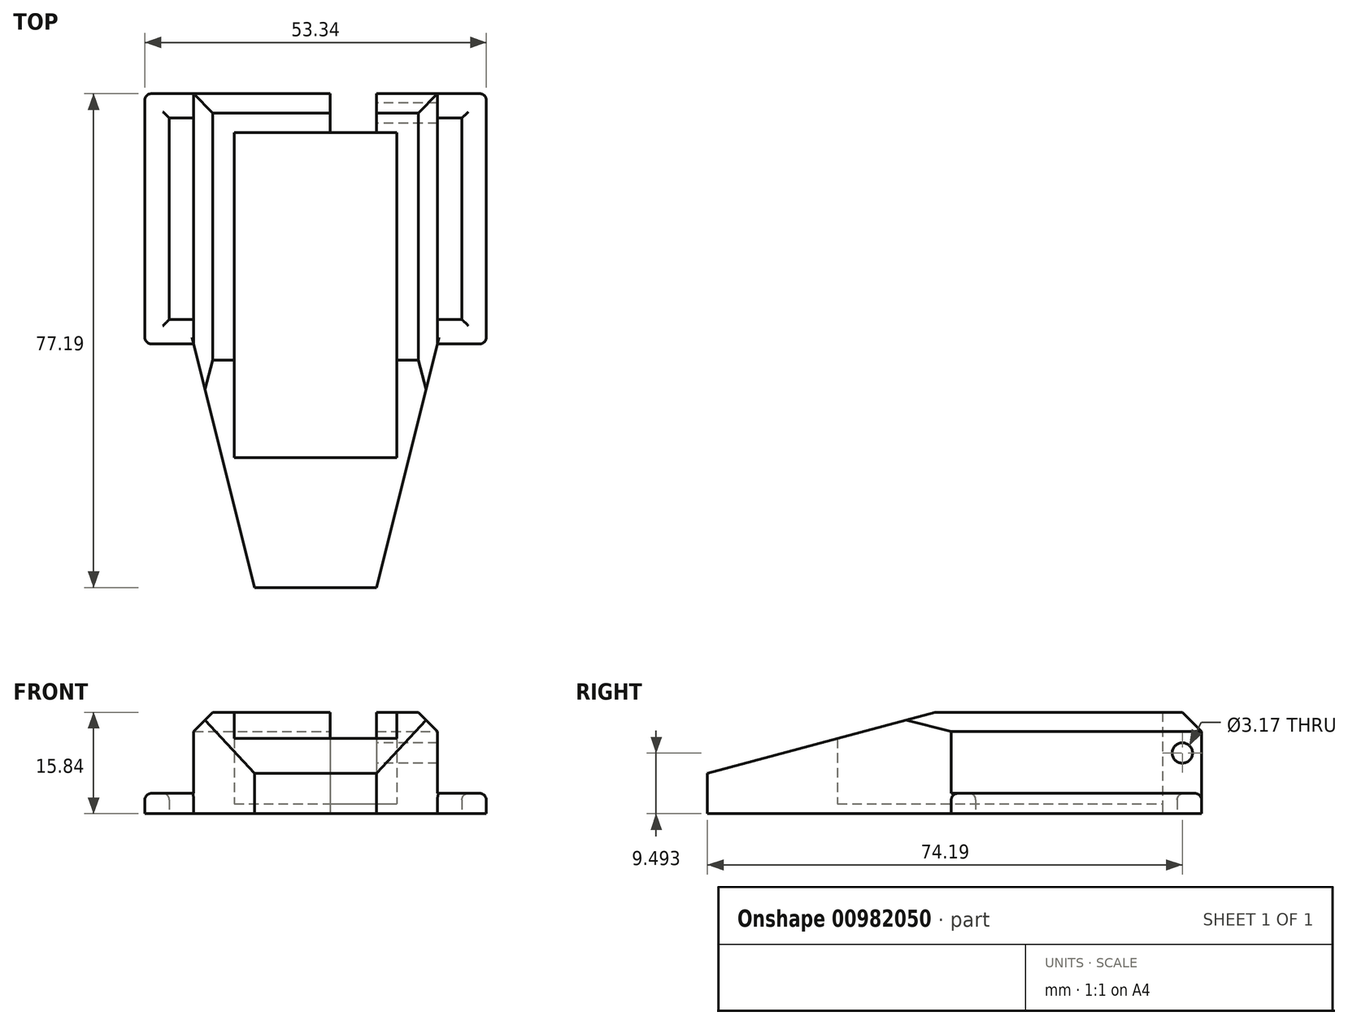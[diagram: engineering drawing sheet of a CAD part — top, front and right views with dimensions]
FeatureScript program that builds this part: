
annotation { "Feature Type Name" : "Feature", "Feature Type Description" : "" }
export const myFeature = defineFeature(function(context is Context, id is Id, definition is map)
    precondition{}
    {
        {
            var Q0;
            Q0=qCreatedBy(makeId("Top.planeOp"),FACE);
            var sketch = newSketch(context, id + "F0", { "sketchPlane" : qUnion([Q0])});
            skLineSegment(sketch, "E0", {"start": v(0, 0) * mm, "end": v(0, 39.09) * mm});
            skLineSegment(sketch, "E1", {"start": v(0, 0) * mm, "end": v(0, -38.1) * mm});
            skLineSegment(sketch, "E2", {"start": v(0, 0) * mm, "end": v(-19.05, 0) * mm});
            skLineSegment(sketch, "E3", {"start": v(0, 0) * mm, "end": v(19.05, 0) * mm});
            skLineSegment(sketch, "E4", {"start": v(-19.05, 0) * mm, "end": v(-19.05, 39.09) * mm});
            skLineSegment(sketch, "E5", {"start": v(19.05, 0) * mm, "end": v(19.05, 39.09) * mm});
            skLineSegment(sketch, "E6", {"start": v(-19.05, 39.09) * mm, "end": v(19.05, 39.09) * mm});
            skLineSegment(sketch, "E7", {"start": v(-19.05, 0) * mm, "end": v(-19.05, -38.1) * mm});
            skLineSegment(sketch, "E8", {"start": v(19.05, 0) * mm, "end": v(19.05, -38.1) * mm});
            skLineSegment(sketch, "E9", {"start": v(-19.05, -38.1) * mm, "end": v(19.05, -38.1) * mm});
            skLineSegment(sketch, "E10", {"start": v(9.53, 0) * mm, "end": v(9.53, 39.09) * mm});
            skLineSegment(sketch, "E11", {"start": v(-9.53, 0) * mm, "end": v(-9.53, 39.09) * mm});
            skLineSegment(sketch, "E12", {"start": v(9.53, 0) * mm, "end": v(9.53, -38.1) * mm});
            skLineSegment(sketch, "E13", {"start": v(-9.53, 0) * mm, "end": v(-9.53, -38.1) * mm});
            skLineSegment(sketch, "E14", {"start": v(-19.05, 19.54) * mm, "end": v(19.05, 19.54) * mm});
            skLineSegment(sketch, "E15", {"start": v(19.05, -19.05) * mm, "end": v(-19.05, -19.05) * mm});
            skLineSegment(sketch, "E16", {"start": v(-19.05, 0) * mm, "end": v(-9.53, -38.1) * mm});
            skLineSegment(sketch, "E17", {"start": v(19.05, 0) * mm, "end": v(9.53, -38.1) * mm});
            skLineSegment(sketch, "E18", {"start": v(0, 0) * mm, "end": v(12.7, 0) * mm});
            skLineSegment(sketch, "E19", {"start": v(0, 0) * mm, "end": v(-12.7, 0) * mm});
            skLineSegment(sketch, "E20", {"start": v(-12.7, 0) * mm, "end": v(-12.7, 33.02) * mm});
            skLineSegment(sketch, "E21", {"start": v(12.7, 0) * mm, "end": v(12.7, 33.02) * mm});
            skLineSegment(sketch, "E22", {"start": v(-12.7, 0) * mm, "end": v(-12.7, -17.78) * mm});
            skLineSegment(sketch, "E23", {"start": v(12.7, 0) * mm, "end": v(12.7, -17.78) * mm});
            skLineSegment(sketch, "E24", {"start": v(-12.7, 33.02) * mm, "end": v(12.7, 33.02) * mm});
            skLineSegment(sketch, "E25", {"start": v(-12.7, -17.78) * mm, "end": v(12.7, -17.78) * mm});
            skLineSegment(sketch, "E26", {"start": v(-19.05, 39.09) * mm, "end": v(-26.67, 39.09) * mm});
            skLineSegment(sketch, "E27", {"start": v(19.05, 39.09) * mm, "end": v(26.67, 39.09) * mm});
            skLineSegment(sketch, "E28", {"start": v(19.05, 0) * mm, "end": v(26.67, 0) * mm});
            skLineSegment(sketch, "E29", {"start": v(-19.05, 0) * mm, "end": v(-26.67, 0) * mm});
            skLineSegment(sketch, "E30", {"start": v(-26.67, 39.09) * mm, "end": v(-26.67, 0) * mm});
            skLineSegment(sketch, "E31", {"start": v(26.67, 39.09) * mm, "end": v(26.67, 0) * mm});
            skLineSegment(sketch, "E32", {"start": v(-19.05, 39.09) * mm, "end": v(-22.86, 39.09) * mm});
            skPoint(sketch, "E32.endSnap0", {"position": v(-22.86, 39.09) * mm});
            skLineSegment(sketch, "E33", {"start": v(-22.86, 39.09) * mm, "end": v(-22.86, 0) * mm});
            skLineSegment(sketch, "E34", {"start": v(19.05, 39.09) * mm, "end": v(22.86, 39.09) * mm});
            skLineSegment(sketch, "E35", {"start": v(22.86, 39.09) * mm, "end": v(22.86, 0) * mm});
            skLineSegment(sketch, "E36", {"start": v(0, 0) * mm, "end": v(0, 3.81) * mm});
            skPoint(sketch, "E36.endSnap0", {"position": v(0, 33.02) * mm});
            skLineSegment(sketch, "E37", {"start": v(0, 3.8) * mm, "end": v(-26.67, 3.8) * mm});
            skLineSegment(sketch, "E38", {"start": v(0, 3.81) * mm, "end": v(26.67, 3.81) * mm});
            skLineSegment(sketch, "E39", {"start": v(0, 39.09) * mm, "end": v(0, 35.28) * mm});
            skLineSegment(sketch, "E40", {"start": v(0, 35.28) * mm, "end": v(26.67, 35.28) * mm});
            skLineSegment(sketch, "E41", {"start": v(0, 35.28) * mm, "end": v(-26.67, 35.28) * mm});
            skLineSegment(sketch, "E42", {"start": v(2.26, 39.09) * mm, "end": v(2.26, 33.02) * mm});
            skSolve(sketch);
        }
        {
            var Q0;
            {var subQ0=sQuery(id+"F0.wireOp",EDGE,"E14");var subQ1=sQuery(id+"F0.wireOp",EDGE,"E0");var subQ2=makeQuery(id+"F0.imprint","INTERSECT",VERTEX,{"derivedFrom":[subQ1,subQ0]});Q0=makeQuery(id+"F0.imprint","IMPRINT",FACE,{"disambiguationData":[TD([[makeQuery(id+"F0.imprint","IMPRINT",EDGE,{"disambiguationData":[TD([[subQ2,-1.0]])],"derivedFrom":subQ1}),1.0]])]});}
            var Q1;
            {var subQ0=sQuery(id+"F0.wireOp",EDGE,"E24");var subQ1=sQuery(id+"F0.wireOp",EDGE,"E11");var subQ2=makeQuery(id+"F0.imprint","INTERSECT",VERTEX,{"derivedFrom":[subQ1,subQ0]});Q1=makeQuery(id+"F0.imprint","IMPRINT",FACE,{"disambiguationData":[TD([[makeQuery(id+"F0.imprint","IMPRINT",EDGE,{"disambiguationData":[TD([[subQ2,1.0]])],"derivedFrom":subQ1}),1.0]])]});}
            var Q2;
            {var subQ0=sQuery(id+"F0.wireOp",EDGE,"E37");var subQ1=sQuery(id+"F0.wireOp",EDGE,"E11");var subQ2=makeQuery(id+"F0.imprint","INTERSECT",VERTEX,{"derivedFrom":[subQ1,subQ0]});Q2=makeQuery(id+"F0.imprint","IMPRINT",FACE,{"disambiguationData":[TD([[makeQuery(id+"F0.imprint","IMPRINT",EDGE,{"disambiguationData":[TD([[subQ2,-1.0]])],"derivedFrom":subQ1}),1.0]])]});}
            var Q3;
            {var subQ0=sQuery(id+"F0.wireOp",EDGE,"E37");var subQ5=sQuery(id+"F0.wireOp",EDGE,"E11");var subQ6=makeQuery(id+"F0.imprint","INTERSECT",VERTEX,{"derivedFrom":[subQ5,subQ0]});Q3=makeQuery(id+"F0.imprint","IMPRINT",FACE,{"disambiguationData":[TD([[makeQuery(id+"F0.imprint","IMPRINT",EDGE,{"disambiguationData":[TD([[subQ6,-1.0]])],"derivedFrom":subQ5}),-1.0]])]});}
            var Q4;
            {var subQ0=sQuery(id+"F0.wireOp",EDGE,"E38");var subQ5=sQuery(id+"F0.wireOp",EDGE,"E10");var subQ6=makeQuery(id+"F0.imprint","INTERSECT",VERTEX,{"derivedFrom":[subQ5,subQ0]});Q4=makeQuery(id+"F0.imprint","IMPRINT",FACE,{"disambiguationData":[TD([[makeQuery(id+"F0.imprint","IMPRINT",EDGE,{"disambiguationData":[TD([[subQ6,-1.0]])],"derivedFrom":subQ5}),1.0]])]});}
            var Q5;
            {var subQ0=sQuery(id+"F0.wireOp",EDGE,"E38");var subQ1=sQuery(id+"F0.wireOp",EDGE,"E10");var subQ2=makeQuery(id+"F0.imprint","INTERSECT",VERTEX,{"derivedFrom":[subQ1,subQ0]});Q5=makeQuery(id+"F0.imprint","IMPRINT",FACE,{"disambiguationData":[TD([[makeQuery(id+"F0.imprint","IMPRINT",EDGE,{"disambiguationData":[TD([[subQ2,-1.0]])],"derivedFrom":subQ1}),-1.0]])]});}
            var Q6;
            {var subQ0=sQuery(id+"F0.wireOp",EDGE,"E14");var subQ1=sQuery(id+"F0.wireOp",EDGE,"E10");var subQ2=makeQuery(id+"F0.imprint","INTERSECT",VERTEX,{"derivedFrom":[subQ1,subQ0]});Q6=makeQuery(id+"F0.imprint","IMPRINT",FACE,{"disambiguationData":[TD([[makeQuery(id+"F0.imprint","IMPRINT",EDGE,{"disambiguationData":[TD([[subQ2,-1.0]])],"derivedFrom":subQ1}),-1.0]])]});}
            var Q7;
            {var subQ4=sQuery(id+"F0.wireOp",EDGE,"E14");var subQ5=sQuery(id+"F0.wireOp",EDGE,"E0");var subQ6=makeQuery(id+"F0.imprint","INTERSECT",VERTEX,{"derivedFrom":[subQ5,subQ4]});Q7=makeQuery(id+"F0.imprint","IMPRINT",FACE,{"disambiguationData":[TD([[makeQuery(id+"F0.imprint","IMPRINT",EDGE,{"disambiguationData":[TD([[subQ6,-1.0]])],"derivedFrom":subQ5}),-1.0]])]});}
            var Q8;
            {var subQ1=sQuery(id+"F0.wireOp",EDGE,"E1");var subQ3=sQuery(id+"F0.wireOp",EDGE,"E25");var subQ4=makeQuery(id+"F0.imprint","INTERSECT",VERTEX,{"derivedFrom":[subQ1,subQ3]});Q8=makeQuery(id+"F0.imprint","IMPRINT",FACE,{"disambiguationData":[TD([[makeQuery(id+"F0.imprint","IMPRINT",EDGE,{"disambiguationData":[TD([[subQ4,1.0]])],"derivedFrom":subQ3}),1.0]])]});}
            var Q9;
            {var subQ1=sQuery(id+"F0.wireOp",EDGE,"E1");var subQ3=sQuery(id+"F0.wireOp",EDGE,"E25");var subQ4=makeQuery(id+"F0.imprint","INTERSECT",VERTEX,{"derivedFrom":[subQ1,subQ3]});Q9=makeQuery(id+"F0.imprint","IMPRINT",FACE,{"disambiguationData":[TD([[makeQuery(id+"F0.imprint","IMPRINT",EDGE,{"disambiguationData":[TD([[subQ4,-1.0]])],"derivedFrom":subQ3}),1.0]])]});}
            var Q10;
            {var subQ0=sQuery(id+"F0.wireOp",EDGE,"E23");Q10=makeQuery(id+"F0.imprint","IMPRINT",FACE,{"disambiguationData":[TD([[makeQuery(id+"F0.imprint","IMPRINT",EDGE,{"derivedFrom":subQ0}),-1.0]])]});}
            var Q11;
            {var subQ0=sQuery(id+"F0.wireOp",EDGE,"E22");Q11=makeQuery(id+"F0.imprint","IMPRINT",FACE,{"disambiguationData":[TD([[makeQuery(id+"F0.imprint","IMPRINT",EDGE,{"derivedFrom":subQ0}),1.0]])]});}
            var Q12;
            {var subQ3=sQuery(id+"F0.wireOp",EDGE,"E11");var subQ5=sQuery(id+"F0.wireOp",EDGE,"E37");var subQ6=makeQuery(id+"F0.imprint","INTERSECT",VERTEX,{"derivedFrom":[subQ3,subQ5]});Q12=makeQuery(id+"F0.imprint","IMPRINT",FACE,{"disambiguationData":[TD([[makeQuery(id+"F0.imprint","IMPRINT",EDGE,{"disambiguationData":[TD([[subQ6,-1.0]])],"derivedFrom":subQ5}),1.0]])]});}
            var Q13;
            {var subQ0=sQuery(id+"F0.wireOp",EDGE,"E37");var subQ5=sQuery(id+"F0.wireOp",EDGE,"E11");var subQ7=makeQuery(id+"F0.imprint","INTERSECT",VERTEX,{"derivedFrom":[subQ5,subQ0]});Q13=makeQuery(id+"F0.imprint","IMPRINT",FACE,{"disambiguationData":[TD([[makeQuery(id+"F0.imprint","IMPRINT",EDGE,{"disambiguationData":[TD([[subQ7,1.0]])],"derivedFrom":subQ5}),-1.0]])]});}
            var Q14;
            {var subQ0=sQuery(id+"F0.wireOp",EDGE,"E38");var subQ5=sQuery(id+"F0.wireOp",EDGE,"E10");var subQ7=makeQuery(id+"F0.imprint","INTERSECT",VERTEX,{"derivedFrom":[subQ5,subQ0]});Q14=makeQuery(id+"F0.imprint","IMPRINT",FACE,{"disambiguationData":[TD([[makeQuery(id+"F0.imprint","IMPRINT",EDGE,{"disambiguationData":[TD([[subQ7,1.0]])],"derivedFrom":subQ5}),1.0]])]});}
            var Q15;
            {var subQ3=sQuery(id+"F0.wireOp",EDGE,"E10");var subQ5=sQuery(id+"F0.wireOp",EDGE,"E38");var subQ6=makeQuery(id+"F0.imprint","INTERSECT",VERTEX,{"derivedFrom":[subQ3,subQ5]});Q15=makeQuery(id+"F0.imprint","IMPRINT",FACE,{"disambiguationData":[TD([[makeQuery(id+"F0.imprint","IMPRINT",EDGE,{"disambiguationData":[TD([[subQ6,-1.0]])],"derivedFrom":subQ5}),-1.0]])]});}
            extrude(context, id + "F1", {"entities" : qUnion([Q0, Q1, Q2, Q3, Q4, Q5, Q6, Q7, Q8, Q9, Q10, Q11, Q12, Q13, Q14, Q15]), "depth" : 1.56 * mm, "offsetDistance" : 25.4 * mm});
        }
        {
            var Q0;
            {var subQ3=sQuery(id+"F0.wireOp",EDGE,"E14");var subQ5=sQuery(id+"F0.wireOp",EDGE,"E4");var subQ6=makeQuery(id+"F0.imprint","INTERSECT",VERTEX,{"derivedFrom":[subQ5,subQ3]});Q0=makeQuery(id+"F0.imprint","IMPRINT",FACE,{"disambiguationData":[TD([[makeQuery(id+"F0.imprint","IMPRINT",EDGE,{"disambiguationData":[TD([[subQ6,-1.0]])],"derivedFrom":subQ5}),-1.0]])]});}
            var Q1;
            {var subQ3=sQuery(id+"F0.wireOp",EDGE,"E41");var subQ5=sQuery(id+"F0.wireOp",EDGE,"E11");var subQ7=makeQuery(id+"F0.imprint","INTERSECT",VERTEX,{"derivedFrom":[subQ5,subQ3]});Q1=makeQuery(id+"F0.imprint","IMPRINT",FACE,{"disambiguationData":[TD([[makeQuery(id+"F0.imprint","IMPRINT",EDGE,{"disambiguationData":[TD([[subQ7,-1.0]])],"derivedFrom":subQ5}),1.0]])]});}
            var Q2;
            {var subQ0=sQuery(id+"F0.wireOp",EDGE,"E26");var subQ5=sQuery(id+"F0.wireOp",EDGE,"E33");var subQ6=makeQuery(id+"F0.imprint","INTERSECT",VERTEX,{"derivedFrom":[subQ0,subQ5]});Q2=makeQuery(id+"F0.imprint","IMPRINT",FACE,{"disambiguationData":[TD([[makeQuery(id+"F0.imprint","IMPRINT",EDGE,{"disambiguationData":[TD([[subQ6,-1.0]])],"derivedFrom":subQ5}),1.0]])]});}
            var Q3;
            {var subQ0=sQuery(id+"F0.wireOp",EDGE,"E33");var subQ1=sQuery(id+"F0.wireOp",EDGE,"E26");var subQ2=makeQuery(id+"F0.imprint","INTERSECT",VERTEX,{"derivedFrom":[subQ1,subQ0]});Q3=makeQuery(id+"F0.imprint","IMPRINT",FACE,{"disambiguationData":[TD([[makeQuery(id+"F0.imprint","IMPRINT",EDGE,{"disambiguationData":[TD([[subQ2,-1.0]])],"derivedFrom":subQ1}),1.0]])]});}
            var Q4;
            {var subQ0=sQuery(id+"F0.wireOp",EDGE,"E41");var subQ1=sQuery(id+"F0.wireOp",EDGE,"E30");var subQ2=makeQuery(id+"F0.imprint","INTERSECT",VERTEX,{"derivedFrom":[subQ1,subQ0]});Q4=makeQuery(id+"F0.imprint","IMPRINT",FACE,{"disambiguationData":[TD([[makeQuery(id+"F0.imprint","IMPRINT",EDGE,{"disambiguationData":[TD([[subQ2,-1.0]])],"derivedFrom":subQ1}),1.0]])]});}
            var Q5;
            {var subQ0=sQuery(id+"F0.wireOp",EDGE,"E30");var subQ1=sQuery(id+"F0.wireOp",EDGE,"E29");var subQ2=makeQuery(id+"F0.imprint","INTERSECT",VERTEX,{"derivedFrom":[subQ1,subQ0]});Q5=makeQuery(id+"F0.imprint","IMPRINT",FACE,{"disambiguationData":[TD([[makeQuery(id+"F0.imprint","IMPRINT",EDGE,{"disambiguationData":[TD([[subQ2,1.0]])],"derivedFrom":subQ1}),-1.0]])]});}
            var Q6;
            {var subQ3=sQuery(id+"F0.wireOp",EDGE,"E29");var subQ5=sQuery(id+"F0.wireOp",EDGE,"E33");var subQ7=makeQuery(id+"F0.imprint","INTERSECT",VERTEX,{"derivedFrom":[subQ3,subQ5]});Q6=makeQuery(id+"F0.imprint","IMPRINT",FACE,{"disambiguationData":[TD([[makeQuery(id+"F0.imprint","IMPRINT",EDGE,{"disambiguationData":[TD([[subQ7,1.0]])],"derivedFrom":subQ5}),1.0]])]});}
            var Q7;
            {var subQ3=sQuery(id+"F0.wireOp",EDGE,"E4");var subQ5=sQuery(id+"F0.wireOp",EDGE,"E37");var subQ7=makeQuery(id+"F0.imprint","INTERSECT",VERTEX,{"derivedFrom":[subQ3,subQ5]});Q7=makeQuery(id+"F0.imprint","IMPRINT",FACE,{"disambiguationData":[TD([[makeQuery(id+"F0.imprint","IMPRINT",EDGE,{"disambiguationData":[TD([[subQ7,1.0]])],"derivedFrom":subQ5}),1.0]])]});}
            var Q8;
            {var subQ0=sQuery(id+"F0.wireOp",EDGE,"E37");var subQ1=sQuery(id+"F0.wireOp",EDGE,"E4");var subQ2=makeQuery(id+"F0.imprint","INTERSECT",VERTEX,{"derivedFrom":[subQ1,subQ0]});Q8=makeQuery(id+"F0.imprint","IMPRINT",FACE,{"disambiguationData":[TD([[makeQuery(id+"F0.imprint","IMPRINT",EDGE,{"disambiguationData":[TD([[subQ2,-1.0]])],"derivedFrom":subQ1}),-1.0]])]});}
            var Q9;
            {var subQ9=sQuery(id+"F0.wireOp",EDGE,"E22");Q9=makeQuery(id+"F0.imprint","IMPRINT",FACE,{"disambiguationData":[TD([[makeQuery(id+"F0.imprint","IMPRINT",EDGE,{"derivedFrom":subQ9}),-1.0]])]});}
            var Q10;
            {var subQ0=sQuery(id+"F0.wireOp",EDGE,"E15");var subQ1=sQuery(id+"F0.wireOp",EDGE,"E1");var subQ2=makeQuery(id+"F0.imprint","INTERSECT",VERTEX,{"derivedFrom":[subQ1,subQ0]});Q10=makeQuery(id+"F0.imprint","IMPRINT",FACE,{"disambiguationData":[TD([[makeQuery(id+"F0.imprint","IMPRINT",EDGE,{"disambiguationData":[TD([[subQ2,1.0]])],"derivedFrom":subQ1}),-1.0]])]});}
            var Q11;
            {var subQ0=sQuery(id+"F0.wireOp",EDGE,"E15");var subQ1=sQuery(id+"F0.wireOp",EDGE,"E1");var subQ2=makeQuery(id+"F0.imprint","INTERSECT",VERTEX,{"derivedFrom":[subQ1,subQ0]});Q11=makeQuery(id+"F0.imprint","IMPRINT",FACE,{"disambiguationData":[TD([[makeQuery(id+"F0.imprint","IMPRINT",EDGE,{"disambiguationData":[TD([[subQ2,1.0]])],"derivedFrom":subQ1}),1.0]])]});}
            var Q12;
            {var subQ9=sQuery(id+"F0.wireOp",EDGE,"E23");Q12=makeQuery(id+"F0.imprint","IMPRINT",FACE,{"disambiguationData":[TD([[makeQuery(id+"F0.imprint","IMPRINT",EDGE,{"derivedFrom":subQ9}),1.0]])]});}
            var Q13;
            {var subQ0=sQuery(id+"F0.wireOp",EDGE,"E15");var subQ1=sQuery(id+"F0.wireOp",EDGE,"E12");var subQ2=makeQuery(id+"F0.imprint","INTERSECT",VERTEX,{"derivedFrom":[subQ1,subQ0]});Q13=makeQuery(id+"F0.imprint","IMPRINT",FACE,{"disambiguationData":[TD([[makeQuery(id+"F0.imprint","IMPRINT",EDGE,{"disambiguationData":[TD([[subQ2,1.0]])],"derivedFrom":subQ0}),1.0]])]});}
            var Q14;
            {var subQ1=sQuery(id+"F0.wireOp",EDGE,"E13");var subQ3=sQuery(id+"F0.wireOp",EDGE,"E15");var subQ4=makeQuery(id+"F0.imprint","INTERSECT",VERTEX,{"derivedFrom":[subQ1,subQ3]});Q14=makeQuery(id+"F0.imprint","IMPRINT",FACE,{"disambiguationData":[TD([[makeQuery(id+"F0.imprint","IMPRINT",EDGE,{"disambiguationData":[TD([[subQ4,-1.0]])],"derivedFrom":subQ3}),1.0]])]});}
            var Q15;
            {var subQ0=sQuery(id+"F0.wireOp",EDGE,"E15");var subQ1=sQuery(id+"F0.wireOp",EDGE,"E1");var subQ2=makeQuery(id+"F0.imprint","INTERSECT",VERTEX,{"derivedFrom":[subQ1,subQ0]});Q15=makeQuery(id+"F0.imprint","IMPRINT",FACE,{"disambiguationData":[TD([[makeQuery(id+"F0.imprint","IMPRINT",EDGE,{"disambiguationData":[TD([[subQ2,-1.0]])],"derivedFrom":subQ1}),-1.0]])]});}
            var Q16;
            {var subQ0=sQuery(id+"F0.wireOp",EDGE,"E15");var subQ1=sQuery(id+"F0.wireOp",EDGE,"E1");var subQ2=makeQuery(id+"F0.imprint","INTERSECT",VERTEX,{"derivedFrom":[subQ1,subQ0]});Q16=makeQuery(id+"F0.imprint","IMPRINT",FACE,{"disambiguationData":[TD([[makeQuery(id+"F0.imprint","IMPRINT",EDGE,{"disambiguationData":[TD([[subQ2,-1.0]])],"derivedFrom":subQ1}),1.0]])]});}
            var Q17;
            {var subQ0=sQuery(id+"F0.wireOp",EDGE,"E21");var subQ5=sQuery(id+"F0.wireOp",EDGE,"E38");var subQ6=makeQuery(id+"F0.imprint","INTERSECT",VERTEX,{"derivedFrom":[subQ0,subQ5]});Q17=makeQuery(id+"F0.imprint","IMPRINT",FACE,{"disambiguationData":[TD([[makeQuery(id+"F0.imprint","IMPRINT",EDGE,{"disambiguationData":[TD([[subQ6,-1.0]])],"derivedFrom":subQ5}),-1.0]])]});}
            var Q18;
            {var subQ0=sQuery(id+"F0.wireOp",EDGE,"E14");var subQ1=sQuery(id+"F0.wireOp",EDGE,"E5");var subQ2=makeQuery(id+"F0.imprint","INTERSECT",VERTEX,{"derivedFrom":[subQ1,subQ0]});Q18=makeQuery(id+"F0.imprint","IMPRINT",FACE,{"disambiguationData":[TD([[makeQuery(id+"F0.imprint","IMPRINT",EDGE,{"disambiguationData":[TD([[subQ2,1.0]])],"derivedFrom":subQ1}),1.0]])]});}
            var Q19;
            {var subQ1=sQuery(id+"F0.wireOp",EDGE,"E14");var subQ5=sQuery(id+"F0.wireOp",EDGE,"E5");var subQ6=makeQuery(id+"F0.imprint","INTERSECT",VERTEX,{"derivedFrom":[subQ5,subQ1]});Q19=makeQuery(id+"F0.imprint","IMPRINT",FACE,{"disambiguationData":[TD([[makeQuery(id+"F0.imprint","IMPRINT",EDGE,{"disambiguationData":[TD([[subQ6,-1.0]])],"derivedFrom":subQ5}),1.0]])]});}
            var Q20;
            {var subQ0=sQuery(id+"F0.wireOp",EDGE,"E41");var subQ5=sQuery(id+"F0.wireOp",EDGE,"E11");var subQ6=makeQuery(id+"F0.imprint","INTERSECT",VERTEX,{"derivedFrom":[subQ5,subQ0]});Q20=makeQuery(id+"F0.imprint","IMPRINT",FACE,{"disambiguationData":[TD([[makeQuery(id+"F0.imprint","IMPRINT",EDGE,{"disambiguationData":[TD([[subQ6,1.0]])],"derivedFrom":subQ5}),-1.0]])]});}
            var Q21;
            {var subQ1=sQuery(id+"F0.wireOp",EDGE,"E0");var subQ3=sQuery(id+"F0.wireOp",EDGE,"E6");var subQ4=makeQuery(id+"F0.imprint","INTERSECT",VERTEX,{"derivedFrom":[subQ1,subQ3]});Q21=makeQuery(id+"F0.imprint","IMPRINT",FACE,{"disambiguationData":[TD([[makeQuery(id+"F0.imprint","IMPRINT",EDGE,{"disambiguationData":[TD([[subQ4,1.0]])],"derivedFrom":subQ3}),-1.0]])]});}
            var Q22;
            {var subQ3=sQuery(id+"F0.wireOp",EDGE,"E6");var subQ5=sQuery(id+"F0.wireOp",EDGE,"E42");var subQ6=makeQuery(id+"F0.imprint","INTERSECT",VERTEX,{"derivedFrom":[subQ3,subQ5]});Q22=makeQuery(id+"F0.imprint","IMPRINT",FACE,{"disambiguationData":[TD([[makeQuery(id+"F0.imprint","IMPRINT",EDGE,{"disambiguationData":[TD([[subQ6,1.0]])],"derivedFrom":subQ3}),-1.0]])]});}
            var Q23;
            {var subQ0=sQuery(id+"F0.wireOp",EDGE,"E6");var subQ5=sQuery(id+"F0.wireOp",EDGE,"E10");var subQ6=makeQuery(id+"F0.imprint","INTERSECT",VERTEX,{"derivedFrom":[subQ0,subQ5]});Q23=makeQuery(id+"F0.imprint","IMPRINT",FACE,{"disambiguationData":[TD([[makeQuery(id+"F0.imprint","IMPRINT",EDGE,{"disambiguationData":[TD([[subQ6,1.0]])],"derivedFrom":subQ5}),-1.0]])]});}
            var Q24;
            {var subQ0=sQuery(id+"F0.wireOp",EDGE,"E27");var subQ5=sQuery(id+"F0.wireOp",EDGE,"E35");var subQ6=makeQuery(id+"F0.imprint","INTERSECT",VERTEX,{"derivedFrom":[subQ0,subQ5]});Q24=makeQuery(id+"F0.imprint","IMPRINT",FACE,{"disambiguationData":[TD([[makeQuery(id+"F0.imprint","IMPRINT",EDGE,{"disambiguationData":[TD([[subQ6,-1.0]])],"derivedFrom":subQ5}),-1.0]])]});}
            var Q25;
            {var subQ0=sQuery(id+"F0.wireOp",EDGE,"E35");var subQ1=sQuery(id+"F0.wireOp",EDGE,"E27");var subQ2=makeQuery(id+"F0.imprint","INTERSECT",VERTEX,{"derivedFrom":[subQ1,subQ0]});Q25=makeQuery(id+"F0.imprint","IMPRINT",FACE,{"disambiguationData":[TD([[makeQuery(id+"F0.imprint","IMPRINT",EDGE,{"disambiguationData":[TD([[subQ2,-1.0]])],"derivedFrom":subQ1}),-1.0]])]});}
            var Q26;
            {var subQ0=sQuery(id+"F0.wireOp",EDGE,"E40");var subQ1=sQuery(id+"F0.wireOp",EDGE,"E31");var subQ2=makeQuery(id+"F0.imprint","INTERSECT",VERTEX,{"derivedFrom":[subQ1,subQ0]});Q26=makeQuery(id+"F0.imprint","IMPRINT",FACE,{"disambiguationData":[TD([[makeQuery(id+"F0.imprint","IMPRINT",EDGE,{"disambiguationData":[TD([[subQ2,-1.0]])],"derivedFrom":subQ1}),-1.0]])]});}
            var Q27;
            {var subQ0=sQuery(id+"F0.wireOp",EDGE,"E35");var subQ1=sQuery(id+"F0.wireOp",EDGE,"E28");var subQ2=makeQuery(id+"F0.imprint","INTERSECT",VERTEX,{"derivedFrom":[subQ1,subQ0]});Q27=makeQuery(id+"F0.imprint","IMPRINT",FACE,{"disambiguationData":[TD([[makeQuery(id+"F0.imprint","IMPRINT",EDGE,{"disambiguationData":[TD([[subQ2,-1.0]])],"derivedFrom":subQ1}),1.0]])]});}
            var Q28;
            {var subQ0=sQuery(id+"F0.wireOp",EDGE,"E28");var subQ5=sQuery(id+"F0.wireOp",EDGE,"E35");var subQ6=makeQuery(id+"F0.imprint","INTERSECT",VERTEX,{"derivedFrom":[subQ0,subQ5]});Q28=makeQuery(id+"F0.imprint","IMPRINT",FACE,{"disambiguationData":[TD([[makeQuery(id+"F0.imprint","IMPRINT",EDGE,{"disambiguationData":[TD([[subQ6,1.0]])],"derivedFrom":subQ5}),-1.0]])]});}
            var Q29;
            {var subQ3=sQuery(id+"F0.wireOp",EDGE,"E24");var subQ5=sQuery(id+"F0.wireOp",EDGE,"E42");var subQ6=makeQuery(id+"F0.imprint","INTERSECT",VERTEX,{"derivedFrom":[subQ3,subQ5]});Q29=makeQuery(id+"F0.imprint","IMPRINT",FACE,{"disambiguationData":[TD([[makeQuery(id+"F0.imprint","IMPRINT",EDGE,{"disambiguationData":[TD([[subQ6,1.0]])],"derivedFrom":subQ3}),1.0]])]});}
            extrude(context, id + "F2", {"entities" : qUnion([Q0, Q1, Q2, Q3, Q4, Q5, Q6, Q7, Q8, Q9, Q10, Q11, Q12, Q13, Q14, Q15, Q16, Q17, Q18, Q19, Q20, Q21, Q22, Q23, Q24, Q25, Q26, Q27, Q28, Q29]), "operationType" : NewBodyOperationType.ADD, "depth" : 3.17 * mm, "offsetDistance" : 25.4 * mm});
        }
        {
            var Q0;
            Q0=makeQuery(id+"F2.opExtrude","CAP_EDGE",EDGE,{"disambiguationData":[OSD([sQuery(id+"F0.wireOp",EDGE,"E31")])],"isStart":false});
            var Q1;
            Q1=makeQuery(id+"F2.opExtrude","CAP_EDGE",EDGE,{"disambiguationData":[OSD([sQuery(id+"F0.wireOp",EDGE,"E28")])],"isStart":false});
            var Q2;
            Q2=makeQuery(id+"F2.opExtrude","SWEPT_EDGE",EDGE,{"disambiguationData":[OSD([sQuery(id+"F0.wireOp",EDGE,"E28"),sQuery(id+"F0.wireOp",EDGE,"E31")])]});
            var Q3;
            Q3=makeQuery(id+"F2.opExtrude","SWEPT_EDGE",EDGE,{"disambiguationData":[OSD([sQuery(id+"F0.wireOp",EDGE,"E27"),sQuery(id+"F0.wireOp",EDGE,"E31")])]});
            var Q4;
            {var subQ0=sQuery(id+"F0.wireOp",EDGE,"E6");Q4=qUnion([makeQuery(id+"F2.opExtrude","CAP_EDGE",EDGE,{"disambiguationData":[OSD([subQ0,sQuery(id+"F0.wireOp",EDGE,"E26")])],"isStart":false}),makeQuery(id+"F2.opExtrude","CAP_EDGE",EDGE,{"disambiguationData":[OSD([subQ0,sQuery(id+"F0.wireOp",EDGE,"E27")])],"isStart":false})]);}
            var Q5;
            Q5=makeQuery(id+"F2.opExtrude","CAP_EDGE",EDGE,{"disambiguationData":[OSD([sQuery(id+"F0.wireOp",EDGE,"E40")])],"isStart":false});
            var Q6;
            Q6=makeQuery(id+"F2.opExtrude","CAP_EDGE",EDGE,{"disambiguationData":[OSD([sQuery(id+"F0.wireOp",EDGE,"E38")])],"isStart":false});
            var Q7;
            Q7=makeQuery(id+"F2.opExtrude","CAP_EDGE",EDGE,{"disambiguationData":[OSD([sQuery(id+"F0.wireOp",EDGE,"E35")])],"isStart":false});
            var Q8;
            Q8=makeQuery(id+"F2.opExtrude","CAP_EDGE",EDGE,{"disambiguationData":[OSD([sQuery(id+"F0.wireOp",EDGE,"E30")])],"isStart":false});
            var Q9;
            Q9=makeQuery(id+"F2.opExtrude","CAP_EDGE",EDGE,{"disambiguationData":[OSD([sQuery(id+"F0.wireOp",EDGE,"E29")])],"isStart":false});
            var Q10;
            Q10=makeQuery(id+"F2.opExtrude","SWEPT_EDGE",EDGE,{"disambiguationData":[OSD([sQuery(id+"F0.wireOp",EDGE,"E29"),sQuery(id+"F0.wireOp",EDGE,"E30")])]});
            var Q11;
            Q11=makeQuery(id+"F2.opExtrude","CAP_EDGE",EDGE,{"disambiguationData":[OSD([sQuery(id+"F0.wireOp",EDGE,"E33")])],"isStart":false});
            var Q12;
            Q12=makeQuery(id+"F2.opExtrude","CAP_EDGE",EDGE,{"disambiguationData":[OSD([sQuery(id+"F0.wireOp",EDGE,"E41")])],"isStart":false});
            var Q13;
            {var subQ0=sQuery(id+"F0.wireOp",EDGE,"E6");Q13=qUnion([makeQuery(id+"F2.opExtrude","CAP_EDGE",EDGE,{"disambiguationData":[OSD([subQ0,sQuery(id+"F0.wireOp",EDGE,"E26")])],"isStart":false}),makeQuery(id+"F2.opExtrude","CAP_EDGE",EDGE,{"disambiguationData":[OSD([subQ0,sQuery(id+"F0.wireOp",EDGE,"E27")])],"isStart":false})]);}
            var Q14;
            Q14=makeQuery(id+"F2.opExtrude","SWEPT_EDGE",EDGE,{"disambiguationData":[OSD([sQuery(id+"F0.wireOp",EDGE,"E26"),sQuery(id+"F0.wireOp",EDGE,"E30")])]});
            var Q15;
            Q15=makeQuery(id+"F2.opExtrude","CAP_EDGE",EDGE,{"disambiguationData":[OSD([sQuery(id+"F0.wireOp",EDGE,"E37")])],"isStart":false});
            fillet(context, id + "F3", {"entities" : qUnion([Q0, Q1, Q2, Q3, Q4, Q5, Q6, Q7, Q8, Q9, Q10, Q11, Q12, Q13, Q14, Q15]), "radius" : 1 * mm, "tangentPropagation" : true, "allowEdgeOverflow" : false});
        }
        {
            var Q0;
            {var subQ3=sQuery(id+"F0.wireOp",EDGE,"E41");var subQ5=sQuery(id+"F0.wireOp",EDGE,"E11");var subQ7=makeQuery(id+"F0.imprint","INTERSECT",VERTEX,{"derivedFrom":[subQ5,subQ3]});Q0=makeQuery(id+"F0.imprint","IMPRINT",FACE,{"disambiguationData":[TD([[makeQuery(id+"F0.imprint","IMPRINT",EDGE,{"disambiguationData":[TD([[subQ7,-1.0]])],"derivedFrom":subQ5}),1.0]])]});}
            var Q1;
            {var subQ3=sQuery(id+"F0.wireOp",EDGE,"E14");var subQ5=sQuery(id+"F0.wireOp",EDGE,"E4");var subQ6=makeQuery(id+"F0.imprint","INTERSECT",VERTEX,{"derivedFrom":[subQ5,subQ3]});Q1=makeQuery(id+"F0.imprint","IMPRINT",FACE,{"disambiguationData":[TD([[makeQuery(id+"F0.imprint","IMPRINT",EDGE,{"disambiguationData":[TD([[subQ6,-1.0]])],"derivedFrom":subQ5}),-1.0]])]});}
            var Q2;
            {var subQ0=sQuery(id+"F0.wireOp",EDGE,"E41");var subQ5=sQuery(id+"F0.wireOp",EDGE,"E11");var subQ6=makeQuery(id+"F0.imprint","INTERSECT",VERTEX,{"derivedFrom":[subQ5,subQ0]});Q2=makeQuery(id+"F0.imprint","IMPRINT",FACE,{"disambiguationData":[TD([[makeQuery(id+"F0.imprint","IMPRINT",EDGE,{"disambiguationData":[TD([[subQ6,1.0]])],"derivedFrom":subQ5}),-1.0]])]});}
            var Q3;
            {var subQ1=sQuery(id+"F0.wireOp",EDGE,"E0");var subQ3=sQuery(id+"F0.wireOp",EDGE,"E6");var subQ4=makeQuery(id+"F0.imprint","INTERSECT",VERTEX,{"derivedFrom":[subQ1,subQ3]});Q3=makeQuery(id+"F0.imprint","IMPRINT",FACE,{"disambiguationData":[TD([[makeQuery(id+"F0.imprint","IMPRINT",EDGE,{"disambiguationData":[TD([[subQ4,1.0]])],"derivedFrom":subQ3}),-1.0]])]});}
            var Q4;
            {var subQ3=sQuery(id+"F0.wireOp",EDGE,"E6");var subQ5=sQuery(id+"F0.wireOp",EDGE,"E42");var subQ6=makeQuery(id+"F0.imprint","INTERSECT",VERTEX,{"derivedFrom":[subQ3,subQ5]});Q4=makeQuery(id+"F0.imprint","IMPRINT",FACE,{"disambiguationData":[TD([[makeQuery(id+"F0.imprint","IMPRINT",EDGE,{"disambiguationData":[TD([[subQ6,1.0]])],"derivedFrom":subQ3}),-1.0]])]});}
            var Q5;
            {var subQ3=sQuery(id+"F0.wireOp",EDGE,"E24");var subQ5=sQuery(id+"F0.wireOp",EDGE,"E42");var subQ6=makeQuery(id+"F0.imprint","INTERSECT",VERTEX,{"derivedFrom":[subQ3,subQ5]});Q5=makeQuery(id+"F0.imprint","IMPRINT",FACE,{"disambiguationData":[TD([[makeQuery(id+"F0.imprint","IMPRINT",EDGE,{"disambiguationData":[TD([[subQ6,1.0]])],"derivedFrom":subQ3}),1.0]])]});}
            var Q6;
            {var subQ0=sQuery(id+"F0.wireOp",EDGE,"E6");var subQ5=sQuery(id+"F0.wireOp",EDGE,"E10");var subQ6=makeQuery(id+"F0.imprint","INTERSECT",VERTEX,{"derivedFrom":[subQ0,subQ5]});Q6=makeQuery(id+"F0.imprint","IMPRINT",FACE,{"disambiguationData":[TD([[makeQuery(id+"F0.imprint","IMPRINT",EDGE,{"disambiguationData":[TD([[subQ6,1.0]])],"derivedFrom":subQ5}),-1.0]])]});}
            var Q7;
            {var subQ1=sQuery(id+"F0.wireOp",EDGE,"E14");var subQ5=sQuery(id+"F0.wireOp",EDGE,"E5");var subQ6=makeQuery(id+"F0.imprint","INTERSECT",VERTEX,{"derivedFrom":[subQ5,subQ1]});Q7=makeQuery(id+"F0.imprint","IMPRINT",FACE,{"disambiguationData":[TD([[makeQuery(id+"F0.imprint","IMPRINT",EDGE,{"disambiguationData":[TD([[subQ6,-1.0]])],"derivedFrom":subQ5}),1.0]])]});}
            var Q8;
            {var subQ0=sQuery(id+"F0.wireOp",EDGE,"E14");var subQ1=sQuery(id+"F0.wireOp",EDGE,"E5");var subQ2=makeQuery(id+"F0.imprint","INTERSECT",VERTEX,{"derivedFrom":[subQ1,subQ0]});Q8=makeQuery(id+"F0.imprint","IMPRINT",FACE,{"disambiguationData":[TD([[makeQuery(id+"F0.imprint","IMPRINT",EDGE,{"disambiguationData":[TD([[subQ2,1.0]])],"derivedFrom":subQ1}),1.0]])]});}
            var Q9;
            {var subQ0=sQuery(id+"F0.wireOp",EDGE,"E21");var subQ5=sQuery(id+"F0.wireOp",EDGE,"E38");var subQ6=makeQuery(id+"F0.imprint","INTERSECT",VERTEX,{"derivedFrom":[subQ0,subQ5]});Q9=makeQuery(id+"F0.imprint","IMPRINT",FACE,{"disambiguationData":[TD([[makeQuery(id+"F0.imprint","IMPRINT",EDGE,{"disambiguationData":[TD([[subQ6,-1.0]])],"derivedFrom":subQ5}),-1.0]])]});}
            var Q10;
            {var subQ9=sQuery(id+"F0.wireOp",EDGE,"E23");Q10=makeQuery(id+"F0.imprint","IMPRINT",FACE,{"disambiguationData":[TD([[makeQuery(id+"F0.imprint","IMPRINT",EDGE,{"derivedFrom":subQ9}),1.0]])]});}
            var Q11;
            {var subQ0=sQuery(id+"F0.wireOp",EDGE,"E15");var subQ1=sQuery(id+"F0.wireOp",EDGE,"E1");var subQ2=makeQuery(id+"F0.imprint","INTERSECT",VERTEX,{"derivedFrom":[subQ1,subQ0]});Q11=makeQuery(id+"F0.imprint","IMPRINT",FACE,{"disambiguationData":[TD([[makeQuery(id+"F0.imprint","IMPRINT",EDGE,{"disambiguationData":[TD([[subQ2,1.0]])],"derivedFrom":subQ1}),1.0]])]});}
            var Q12;
            {var subQ0=sQuery(id+"F0.wireOp",EDGE,"E15");var subQ1=sQuery(id+"F0.wireOp",EDGE,"E1");var subQ2=makeQuery(id+"F0.imprint","INTERSECT",VERTEX,{"derivedFrom":[subQ1,subQ0]});Q12=makeQuery(id+"F0.imprint","IMPRINT",FACE,{"disambiguationData":[TD([[makeQuery(id+"F0.imprint","IMPRINT",EDGE,{"disambiguationData":[TD([[subQ2,1.0]])],"derivedFrom":subQ1}),-1.0]])]});}
            var Q13;
            {var subQ9=sQuery(id+"F0.wireOp",EDGE,"E22");Q13=makeQuery(id+"F0.imprint","IMPRINT",FACE,{"disambiguationData":[TD([[makeQuery(id+"F0.imprint","IMPRINT",EDGE,{"derivedFrom":subQ9}),-1.0]])]});}
            var Q14;
            {var subQ0=sQuery(id+"F0.wireOp",EDGE,"E37");var subQ1=sQuery(id+"F0.wireOp",EDGE,"E4");var subQ2=makeQuery(id+"F0.imprint","INTERSECT",VERTEX,{"derivedFrom":[subQ1,subQ0]});Q14=makeQuery(id+"F0.imprint","IMPRINT",FACE,{"disambiguationData":[TD([[makeQuery(id+"F0.imprint","IMPRINT",EDGE,{"disambiguationData":[TD([[subQ2,-1.0]])],"derivedFrom":subQ1}),-1.0]])]});}
            var Q15;
            {var subQ3=sQuery(id+"F0.wireOp",EDGE,"E4");var subQ5=sQuery(id+"F0.wireOp",EDGE,"E37");var subQ7=makeQuery(id+"F0.imprint","INTERSECT",VERTEX,{"derivedFrom":[subQ3,subQ5]});Q15=makeQuery(id+"F0.imprint","IMPRINT",FACE,{"disambiguationData":[TD([[makeQuery(id+"F0.imprint","IMPRINT",EDGE,{"disambiguationData":[TD([[subQ7,1.0]])],"derivedFrom":subQ5}),1.0]])]});}
            var Q16;
            {var subQ1=sQuery(id+"F0.wireOp",EDGE,"E13");var subQ3=sQuery(id+"F0.wireOp",EDGE,"E15");var subQ4=makeQuery(id+"F0.imprint","INTERSECT",VERTEX,{"derivedFrom":[subQ1,subQ3]});Q16=makeQuery(id+"F0.imprint","IMPRINT",FACE,{"disambiguationData":[TD([[makeQuery(id+"F0.imprint","IMPRINT",EDGE,{"disambiguationData":[TD([[subQ4,-1.0]])],"derivedFrom":subQ3}),1.0]])]});}
            var Q17;
            {var subQ0=sQuery(id+"F0.wireOp",EDGE,"E15");var subQ1=sQuery(id+"F0.wireOp",EDGE,"E12");var subQ2=makeQuery(id+"F0.imprint","INTERSECT",VERTEX,{"derivedFrom":[subQ1,subQ0]});Q17=makeQuery(id+"F0.imprint","IMPRINT",FACE,{"disambiguationData":[TD([[makeQuery(id+"F0.imprint","IMPRINT",EDGE,{"disambiguationData":[TD([[subQ2,1.0]])],"derivedFrom":subQ0}),1.0]])]});}
            var Q18;
            {var subQ0=sQuery(id+"F0.wireOp",EDGE,"E15");var subQ1=sQuery(id+"F0.wireOp",EDGE,"E1");var subQ2=makeQuery(id+"F0.imprint","INTERSECT",VERTEX,{"derivedFrom":[subQ1,subQ0]});Q18=makeQuery(id+"F0.imprint","IMPRINT",FACE,{"disambiguationData":[TD([[makeQuery(id+"F0.imprint","IMPRINT",EDGE,{"disambiguationData":[TD([[subQ2,-1.0]])],"derivedFrom":subQ1}),1.0]])]});}
            var Q19;
            {var subQ0=sQuery(id+"F0.wireOp",EDGE,"E15");var subQ1=sQuery(id+"F0.wireOp",EDGE,"E1");var subQ2=makeQuery(id+"F0.imprint","INTERSECT",VERTEX,{"derivedFrom":[subQ1,subQ0]});Q19=makeQuery(id+"F0.imprint","IMPRINT",FACE,{"disambiguationData":[TD([[makeQuery(id+"F0.imprint","IMPRINT",EDGE,{"disambiguationData":[TD([[subQ2,-1.0]])],"derivedFrom":subQ1}),-1.0]])]});}
            extrude(context, id + "F4", {"entities" : qUnion([Q0, Q1, Q2, Q3, Q4, Q5, Q6, Q7, Q8, Q9, Q10, Q11, Q12, Q13, Q14, Q15, Q16, Q17, Q18, Q19]), "operationType" : NewBodyOperationType.ADD, "depth" : 15.84 * mm, "offsetDistance" : 25.4 * mm});
        }
        {
            var Q0;
            Q0=makeQuery(id+"F4.opExtrude","CAP_EDGE",EDGE,{"disambiguationData":[OSD([sQuery(id+"F0.wireOp",EDGE,"E4")])],"isStart":false});
            var Q1;
            {var subQ0=sQuery(id+"F0.wireOp",EDGE,"E6");var subQ1=makeQuery(id+"F0.imprint","INTERSECT",VERTEX,{"derivedFrom":[sQuery(id+"F0.wireOp",EDGE,"E0"),subQ0]});var subQ2=makeQuery(id+"F0.imprint","INTERSECT",VERTEX,{"derivedFrom":[subQ0,sQuery(id+"F0.wireOp",EDGE,"E11")]});Q1=makeQuery(id+"F4.opExtrude","CAP_EDGE",EDGE,{"disambiguationData":[OSD([subQ0]),TDD([makeQuery(id+"F0.imprint","IMPRINT",EDGE,{"disambiguationData":[TD([[subQ1,1.0]])],"derivedFrom":subQ0}),makeQuery(id+"F0.imprint","IMPRINT",EDGE,{"disambiguationData":[TD([[subQ2,1.0]])],"derivedFrom":subQ0}),makeQuery(id+"F0.imprint","IMPRINT",EDGE,{"disambiguationData":[TD([[makeQuery(id+"F0.imprint","INTERSECT",VERTEX,{"derivedFrom":[subQ0,sQuery(id+"F0.wireOp",EDGE,"E42")]}),1.0]])],"derivedFrom":subQ0})])],"isStart":false});}
            var Q2;
            {var subQ0=sQuery(id+"F0.wireOp",EDGE,"E6");Q2=makeQuery(id+"F4.opExtrude","CAP_EDGE",EDGE,{"disambiguationData":[OSD([subQ0]),TDD([makeQuery(id+"F0.imprint","IMPRINT",EDGE,{"disambiguationData":[TD([[makeQuery(id+"F0.imprint","INTERSECT",VERTEX,{"derivedFrom":[subQ0,sQuery(id+"F0.wireOp",EDGE,"E10")]}),-1.0]])],"derivedFrom":subQ0})])],"isStart":false});}
            var Q3;
            Q3=makeQuery(id+"F4.opExtrude","CAP_EDGE",EDGE,{"disambiguationData":[OSD([sQuery(id+"F0.wireOp",EDGE,"E5")])],"isStart":false});
            chamfer(context, id + "F5", {"entities" : qUnion([Q0, Q1, Q2, Q3]), "width" : 3 * mm, "tangentPropagation" : true});
        }
        {
            var Q0;
            Q0=makeQuery(id+"F4.opExtrude","CAP_EDGE",EDGE,{"disambiguationData":[OSD([sQuery(id+"F0.wireOp",EDGE,"E9")])],"isStart":false});
            chamfer(context, id + "F6", {"entities" : qUnion([Q0]), "chamferType" : ChamferType.OFFSET_ANGLE, "width" : 35.56 * mm, "oppositeDirection" : false, "angle" : 15 * degree, "tangentPropagation" : true});
        }
        {
            var Q0;
            {var subQ0=sQuery(id+"F0.wireOp",EDGE,"E10");Q0=makeQuery(id+"F4.boolean.opBoolean","MERGE",FACE,{"derivedFrom":[makeQuery(id+"F2.opExtrude","SWEPT_FACE",FACE,{"disambiguationData":[OSD([subQ0])]}),makeQuery(id+"F4.opExtrude","SWEPT_FACE",FACE,{"disambiguationData":[OSD([subQ0])]})]});}
            var sketch = newSketch(context, id + "F7", { "sketchPlane" : qUnion([Q0])});
            skLineSegment(sketch, "E43", {"start": v(-36.09, 15.84) * mm, "end": v(-36.09, 9.5) * mm});
            skCircle(sketch, "E44", {"center": v(-36.09, 9.5) * mm, "radius": 1.59 * mm});
            skSolve(sketch);
        }
        {
            var Q0;
            Q0=makeQuery(id+"F7.imprint","IMPRINT",FACE,{"disambiguationData":[TD([[makeQuery(id+"F7.imprint","IMPRINT",EDGE,{"derivedFrom":sQuery(id+"F7.wireOp",EDGE,"E44")}),1.0]])]});
            extrude(context, id + "F8", {"entities" : qUnion([Q0]), "operationType" : NewBodyOperationType.REMOVE, "oppositeDirection" : true, "depth" : 25.4 * mm, "offsetDistance" : 25.4 * mm});
        }
    });
